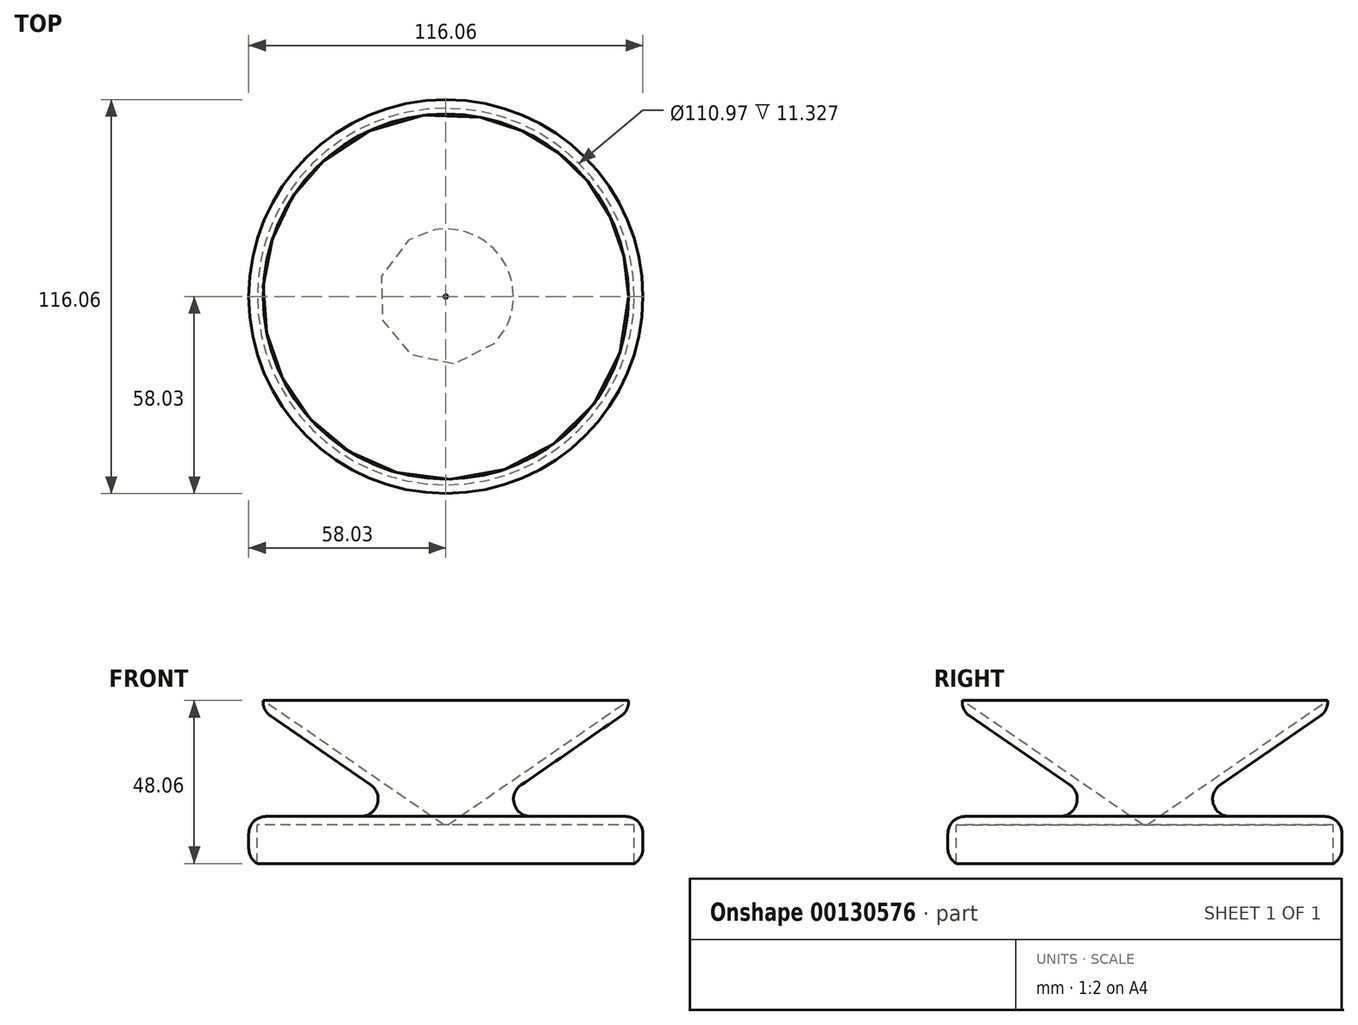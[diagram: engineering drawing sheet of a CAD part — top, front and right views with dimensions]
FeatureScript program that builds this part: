
annotation { "Feature Type Name" : "Feature", "Feature Type Description" : "" }
export const myFeature = defineFeature(function(context is Context, id is Id, definition is map)
    precondition{}
    {
        {
            var Q0;
            Q0=qCreatedBy(makeId("Front.planeOp"),FACE);
            var sketch = newSketch(context, id + "F0", { "sketchPlane" : qUnion([Q0])});
            skLineSegment(sketch, "E0.bottom", {"start": v(0, 0) * mm, "end": v(-58.03, 0) * mm});
            skLineSegment(sketch, "E0.top", {"start": v(0, 13.87) * mm, "end": v(-58.03, 13.87) * mm});
            skLineSegment(sketch, "E0.left", {"start": v(0, 0) * mm, "end": v(0, 13.87) * mm});
            skLineSegment(sketch, "E0.right", {"start": v(-58.03, 0) * mm, "end": v(-58.03, 13.87) * mm});
            skLineSegment(sketch, "E1", {"start": v(0, 48.06) * mm, "end": v(-58.28, 48.06) * mm});
            skLineSegment(sketch, "E2", {"start": v(0, 48.06) * mm, "end": v(0, 13.87) * mm});
            skLineSegment(sketch, "E3", {"start": v(-58.28, 48.06) * mm, "end": v(-8.7, 13.87) * mm});
            skSolve(sketch);
        }
        {
            var Q0;
            Q0=makeQuery(id+"F0.imprint","IMPRINT",FACE,{"disambiguationData":[TD([[makeQuery(id+"F0.imprint","IMPRINT",EDGE,{"derivedFrom":sQuery(id+"F0.wireOp",EDGE,"E1")}),1.0]])]});
            var Q1;
            Q1=makeQuery(id+"F0.imprint","IMPRINT",FACE,{"disambiguationData":[TD([[makeQuery(id+"F0.imprint","IMPRINT",EDGE,{"derivedFrom":sQuery(id+"F0.wireOp",EDGE,"E0.bottom")}),-1.0]])]});
            var Q2;
            Q2=sQuery(id+"F0.wireOp",EDGE,"E2");
            revolve(context, id + "F1", {"entities" : qUnion([Q0, Q1]), "axis" : qUnion([Q2]), "revolveType" : RevolveType.FULL});
        }
        {
            var Q0;
            Q0=makeQuery(id+"F1.opRevolve","SWEPT_FACE",FACE,{"disambiguationData":[OSD([sQuery(id+"F0.wireOp",EDGE,"E1")])]});
            var Q1;
            Q1=makeQuery(id+"F1.opRevolve","SWEPT_FACE",FACE,{"disambiguationData":[OSD([sQuery(id+"F0.wireOp",EDGE,"E0.bottom")])]});
            shell(context, id + "F2", {"entities" : qUnion([Q0, Q1]), "thickness" : 2.54 * mm});
        }
        {
            var Q0;
            Q0=makeQuery(id+"F1.opRevolve","SWEPT_FACE",FACE,{"disambiguationData":[OSD([sQuery(id+"F0.wireOp",EDGE,"E0.right")])]});
            var Q1;
            Q1=makeQuery(id+"F1.opRevolve","SWEPT_FACE",FACE,{"disambiguationData":[OSD([sQuery(id+"F0.wireOp",EDGE,"E3")])]});
            fillet(context, id + "F3", {"entities" : qUnion([Q0, Q1]), "radius" : 5.08 * mm, "tangentPropagation" : true, "allowEdgeOverflow" : false});
        }
    });
